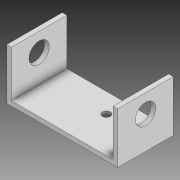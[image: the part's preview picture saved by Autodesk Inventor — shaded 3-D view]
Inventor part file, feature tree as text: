
AUTODESK INVENTOR PART (.ipt)
format: ipt  version: 2020 (Build 240168000, 168)  size: 106,496 bytes
history: native  units: mm
features: extrude x3, sketch x3
ambient origin geometry x8: Origin, YZ Plane, XZ Plane, XY Plane, X Axis, Y Axis, Z Axis, Center Point
bodies: Solid1 (feature_tree)
feature tree (6):
  extrude  "Extrusion1"  Depth=50.0mm
  extrude  "Extrusion2"  Depth=5.0mm
  extrude  "Extrusion3"  Depth=60.0mm
  sketch  "Sketch1"  dims[d0=5.0mm d1=50.0mm]
  sketch  "Sketch2"  dims[d2=120.0mm d3=5.0mm]
  sketch  "Sketch3"  dims[d4=60.0mm d5=0.0mm d6=22.0mm d7=20.0mm d8=0.0mm d9=0.0mm d10=0.0mm d11=0.0mm]
